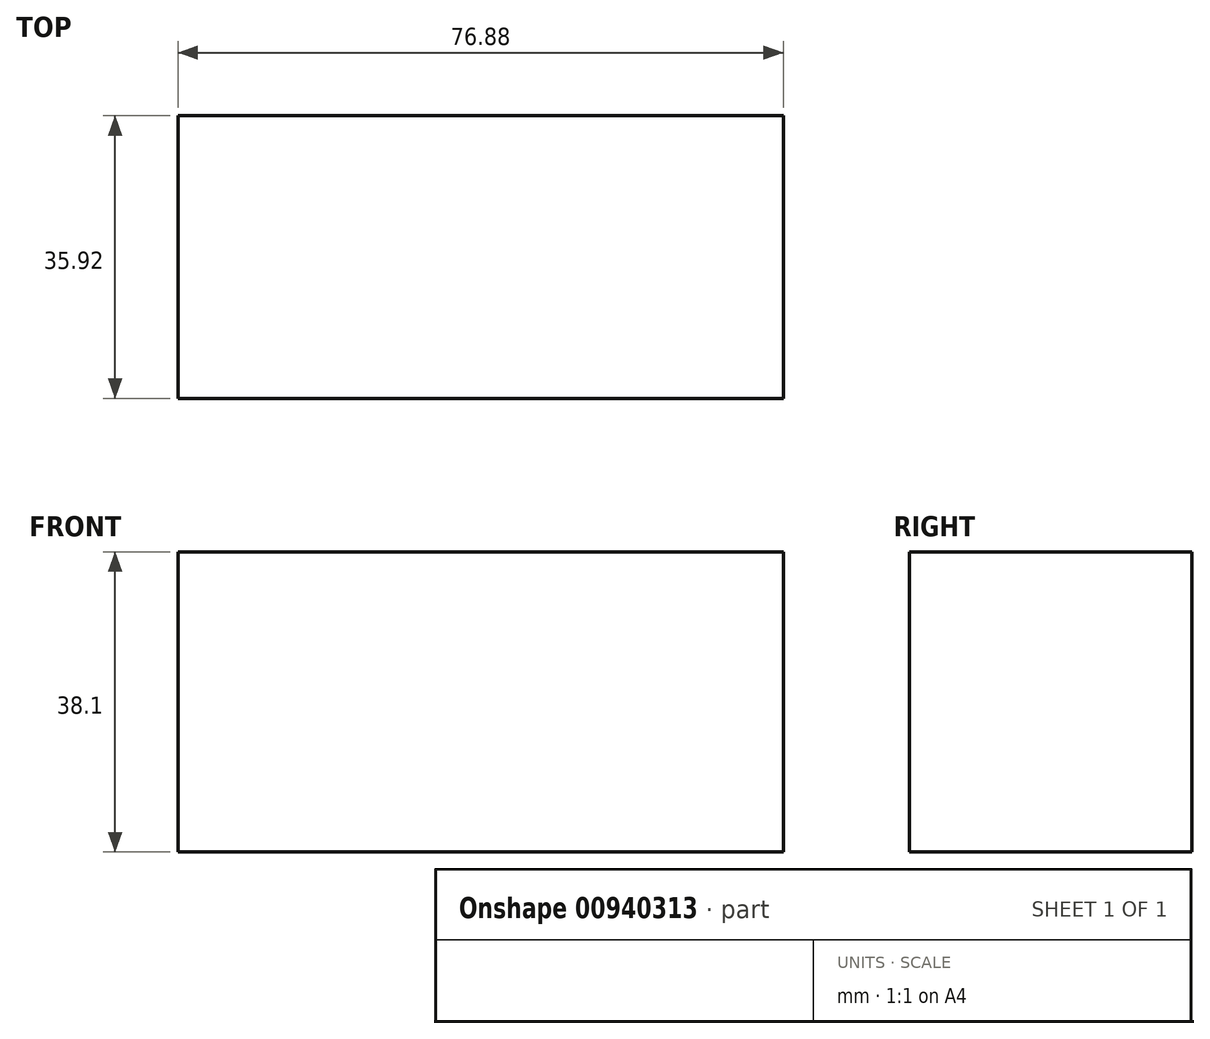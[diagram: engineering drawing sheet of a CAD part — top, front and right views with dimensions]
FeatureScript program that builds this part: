
annotation { "Feature Type Name" : "Feature", "Feature Type Description" : "" }
export const myFeature = defineFeature(function(context is Context, id is Id, definition is map)
    precondition{}
    {
        {
            var Q0;
            Q0=qCreatedBy(makeId("Top.planeOp"),FACE);
            var sketch = newSketch(context, id + "F0", { "sketchPlane" : qUnion([Q0])});
            skLineSegment(sketch, "E0.bottom", {"start": v(-38.44, -17.96) * mm, "end": v(38.44, -17.96) * mm});
            skLineSegment(sketch, "E0.top", {"start": v(-38.44, 17.96) * mm, "end": v(38.44, 17.96) * mm});
            skLineSegment(sketch, "E0.left", {"start": v(-38.44, -17.96) * mm, "end": v(-38.44, 17.96) * mm});
            skLineSegment(sketch, "E0.right", {"start": v(38.44, -17.96) * mm, "end": v(38.44, 17.96) * mm});
            skPoint(sketch, "E0.middle", {"position": v(0, 0) * mm});
            skSolve(sketch);
        }
        {
            var Q0;
            Q0 = qSketchRegion(id + "F0", true);
            extrude(context, id + "F1", {"entities" : qUnion([Q0]), "depth" : 38.1 * mm, "offsetDistance" : 25.4 * mm});
        }
    });
